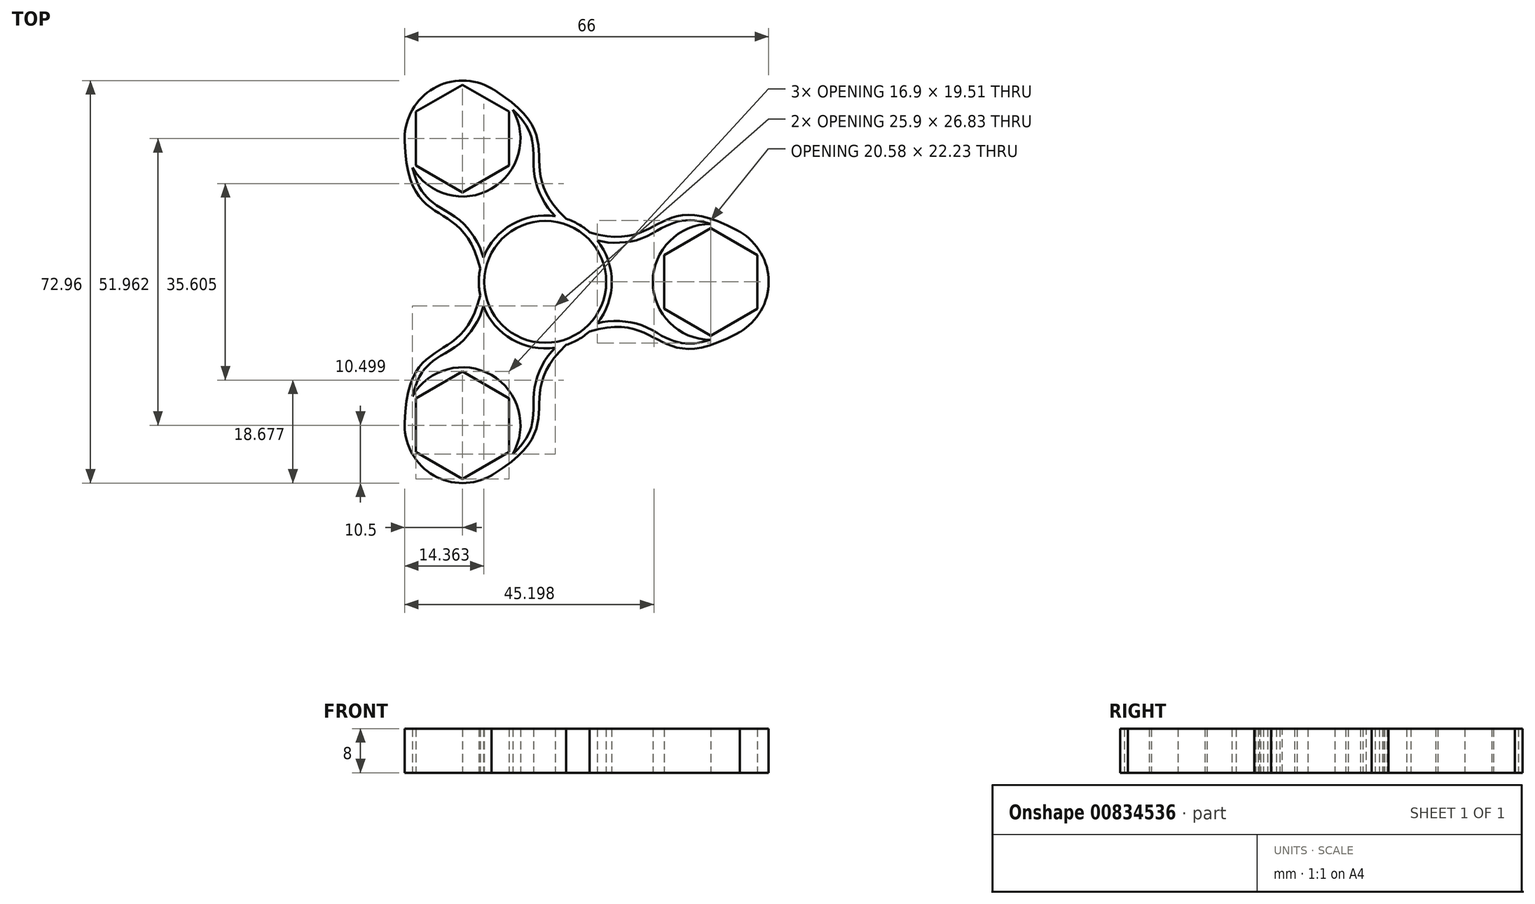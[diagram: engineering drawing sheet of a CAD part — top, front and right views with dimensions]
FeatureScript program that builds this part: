
annotation { "Feature Type Name" : "Feature", "Feature Type Description" : "" }
export const myFeature = defineFeature(function(context is Context, id is Id, definition is map)
    precondition{}
    {
        {
            var Q0;
            Q0=qCreatedBy(makeId("Top.planeOp"),FACE);
            var sketch = newSketch(context, id + "F0", { "sketchPlane" : qUnion([Q0])});
            skCircle(sketch, "E0", {"center": v(0, 0) * mm, "radius": 11.05 * mm});
            skCircle(sketch, "E1.cCircle", {"center": v(30, 0) * mm, "radius": 8.45 * mm, "construction": true});
            skLineSegment(sketch, "E1.0", {"start": v(30, 9.76) * mm, "end": v(38.45, 4.88) * mm});
            skLineSegment(sketch, "E1.1", {"start": v(38.45, 4.88) * mm, "end": v(38.45, -4.88) * mm});
            skLineSegment(sketch, "E1.2", {"start": v(38.45, -4.88) * mm, "end": v(30, -9.76) * mm});
            skLineSegment(sketch, "E1.3", {"start": v(30, -9.76) * mm, "end": v(21.55, -4.88) * mm});
            skLineSegment(sketch, "E1.4", {"start": v(21.55, -4.88) * mm, "end": v(21.55, 4.88) * mm});
            skLineSegment(sketch, "E1.5", {"start": v(21.55, 4.88) * mm, "end": v(30, 9.76) * mm});
            skPoint(sketch, "E1.0.midPoint", {"position": v(34.23, 7.32) * mm});
            skLineSegment(sketch, "E2.1.0", {"start": v(-15, 16.22) * mm, "end": v(-23.45, 21.1) * mm});
            skLineSegment(sketch, "E2.1.1", {"start": v(-6.55, 21.1) * mm, "end": v(-15, 16.22) * mm});
            skLineSegment(sketch, "E2.1.2", {"start": v(-23.45, 21.1) * mm, "end": v(-23.45, 30.86) * mm});
            skLineSegment(sketch, "E2.1.3", {"start": v(-23.45, 30.86) * mm, "end": v(-15, 35.74) * mm});
            skLineSegment(sketch, "E2.1.4", {"start": v(-15, 35.74) * mm, "end": v(-6.55, 30.86) * mm});
            skLineSegment(sketch, "E2.1.5", {"start": v(-6.55, 30.86) * mm, "end": v(-6.55, 21.1) * mm});
            skLineSegment(sketch, "E2.2.0", {"start": v(-6.55, -21.1) * mm, "end": v(-6.55, -30.86) * mm});
            skLineSegment(sketch, "E2.2.1", {"start": v(-15, -16.22) * mm, "end": v(-6.55, -21.1) * mm});
            skLineSegment(sketch, "E2.2.2", {"start": v(-6.55, -30.86) * mm, "end": v(-15, -35.74) * mm});
            skLineSegment(sketch, "E2.2.3", {"start": v(-15, -35.74) * mm, "end": v(-23.45, -30.86) * mm});
            skLineSegment(sketch, "E2.2.4", {"start": v(-23.45, -30.86) * mm, "end": v(-23.45, -21.1) * mm});
            skLineSegment(sketch, "E2.2.5", {"start": v(-23.45, -21.1) * mm, "end": v(-15, -16.22) * mm});
            skSolve(sketch);
        }
        {
            var Q0;
            Q0=qCreatedBy(makeId("Top.planeOp"),FACE);
            var sketch = newSketch(context, id + "F1", { "sketchPlane" : qUnion([Q0])});
            skLineSegment(sketch, "E3.0.0", {"start": v(-6.55, 21.1) * mm, "end": v(-6.55, 30.86) * mm});
            skLineSegment(sketch, "E3.0.1", {"start": v(-6.55, 30.86) * mm, "end": v(-15, 35.74) * mm});
            skLineSegment(sketch, "E3.0.2", {"start": v(-15, 35.74) * mm, "end": v(-23.45, 30.86) * mm});
            skLineSegment(sketch, "E3.0.3", {"start": v(-23.45, 30.86) * mm, "end": v(-23.45, 21.1) * mm});
            skLineSegment(sketch, "E3.0.4", {"start": v(-23.45, 21.1) * mm, "end": v(-15, 16.22) * mm});
            skLineSegment(sketch, "E3.0.5", {"start": v(-15, 16.22) * mm, "end": v(-6.55, 21.1) * mm});
            skCircle(sketch, "E4.0.0", {"center": v(0, 0) * mm, "radius": 11.05 * mm});
            skLineSegment(sketch, "E5.0.0", {"start": v(30, 9.76) * mm, "end": v(21.55, 4.88) * mm});
            skLineSegment(sketch, "E5.0.1", {"start": v(21.55, 4.88) * mm, "end": v(21.55, -4.88) * mm});
            skLineSegment(sketch, "E5.0.2", {"start": v(21.55, -4.88) * mm, "end": v(30, -9.76) * mm});
            skLineSegment(sketch, "E5.0.3", {"start": v(30, -9.76) * mm, "end": v(38.45, -4.88) * mm});
            skLineSegment(sketch, "E5.0.4", {"start": v(38.45, -4.88) * mm, "end": v(38.45, 4.88) * mm});
            skLineSegment(sketch, "E5.0.5", {"start": v(38.45, 4.88) * mm, "end": v(30, 9.76) * mm});
            skLineSegment(sketch, "E6.0.0", {"start": v(-15, -16.22) * mm, "end": v(-23.45, -21.1) * mm});
            skLineSegment(sketch, "E6.0.1", {"start": v(-23.45, -21.1) * mm, "end": v(-23.45, -30.86) * mm});
            skLineSegment(sketch, "E6.0.2", {"start": v(-23.45, -30.86) * mm, "end": v(-15, -35.74) * mm});
            skLineSegment(sketch, "E6.0.3", {"start": v(-15, -35.74) * mm, "end": v(-6.55, -30.86) * mm});
            skLineSegment(sketch, "E6.0.4", {"start": v(-6.55, -30.86) * mm, "end": v(-6.55, -21.1) * mm});
            skLineSegment(sketch, "E6.0.5", {"start": v(-6.55, -21.1) * mm, "end": v(-15, -16.22) * mm});
            skPoint(sketch, "E7.0", {"position": v(30, 0) * mm});
            skCircle(sketch, "E8", {"center": v(30, 0) * mm, "radius": 10.5 * mm});
            skLineSegment(sketch, "E9", {"start": v(34.23, 7.32) * mm, "end": v(35.25, 9.1) * mm, "construction": true});
            skCircle(sketch, "E10.0", {"center": v(0, 0) * mm, "radius": 12.05 * mm});
            skLineSegment(sketch, "E11", {"start": v(8.01, 9) * mm, "end": v(8.01, -9) * mm, "construction": true});
            skFitSpline(sketch, "E12", {"points": [v(8.01, 9) * mm, v(35.25, 9.1) * mm], "startDerivative": vector(40.61, -12.36) * mm, "endDerivative": vector(46.42, -25.85) * mm});
            skLineSegment(sketch, "E13", {"start": v(34.22, -7.32) * mm, "end": v(35.25, -9.1) * mm, "construction": true});
            skFitSpline(sketch, "E14", {"points": [v(8.01, -9) * mm, v(35.25, -9.1) * mm], "startDerivative": vector(40.61, 12.36) * mm, "endDerivative": vector(46.43, 25.85) * mm});
            skLineSegment(sketch, "E15", {"start": v(-6.55, -30.86) * mm, "end": v(-23.45, -21.1) * mm, "construction": true});
            skCircle(sketch, "E16", {"center": v(-15, -25.98) * mm, "radius": 10.5 * mm});
            skLineSegment(sketch, "E17", {"start": v(-11.8, -2.44) * mm, "end": v(3.79, -11.44) * mm, "construction": true});
            skLineSegment(sketch, "E18", {"start": v(-23.45, -25.98) * mm, "end": v(-25.5, -25.98) * mm, "construction": true});
            skLineSegment(sketch, "E19", {"start": v(-10.78, -33.3) * mm, "end": v(-9.75, -35.07) * mm, "construction": true});
            skFitSpline(sketch, "E20", {"points": [v(-25.5, -25.98) * mm, v(-11.8, -2.44) * mm], "startDerivative": vector(0.82, 53.13) * mm, "endDerivative": vector(9.6, 41.35) * mm});
            skLineSegment(sketch, "E21", {"start": v(-25.23, -8.27) * mm, "end": v(-19.23, -18.66) * mm, "construction": true});
            skFitSpline(sketch, "E22", {"points": [v(3.79, -11.44) * mm, v(-9.75, -35.07) * mm], "startDerivative": vector(-31.01, -28.99) * mm, "endDerivative": vector(-45.6, -27.28) * mm});
            skLineSegment(sketch, "E23", {"start": v(-6.55, -25.98) * mm, "end": v(5.45, -25.98) * mm, "construction": true});
            skLineSegment(sketch, "E24", {"start": v(25.77, 7.32) * mm, "end": v(19.78, 17.71) * mm, "construction": true});
            skLineSegment(sketch, "E25", {"start": v(25.77, -7.32) * mm, "end": v(19.77, -17.71) * mm, "construction": true});
            skLineSegment(sketch, "E26", {"start": v(-23.45, 21.1) * mm, "end": v(-6.55, 30.86) * mm, "construction": true});
            skCircle(sketch, "E27", {"center": v(-15, 25.98) * mm, "radius": 10.5 * mm});
            skLineSegment(sketch, "E28", {"start": v(-19.22, 18.66) * mm, "end": v(-25.23, 8.27) * mm, "construction": true});
            skLineSegment(sketch, "E29", {"start": v(-6.55, 25.98) * mm, "end": v(5.45, 25.98) * mm, "construction": true});
            skLineSegment(sketch, "E30", {"start": v(-10.78, 33.3) * mm, "end": v(-9.75, 35.07) * mm, "construction": true});
            skLineSegment(sketch, "E31", {"start": v(-23.45, 25.98) * mm, "end": v(-25.5, 25.98) * mm, "construction": true});
            skLineSegment(sketch, "E32", {"start": v(-11.8, 2.44) * mm, "end": v(3.79, 11.44) * mm, "construction": true});
            skFitSpline(sketch, "E33", {"points": [v(-9.75, 35.07) * mm, v(3.79, 11.44) * mm], "startDerivative": vector(45.6, -27.28) * mm, "endDerivative": vector(31.01, -28.99) * mm});
            skFitSpline(sketch, "E34", {"points": [v(-25.5, 25.98) * mm, v(-11.8, 2.44) * mm], "startDerivative": vector(0.82, -53.13) * mm, "endDerivative": vector(9.6, -41.35) * mm});
            skFitSpline(sketch, "E35.0", {"points": [v(-10.26, 34.22) * mm, v(-8.4, 33.1) * mm, v(-6.27, 31.55) * mm, v(-4.43, 29.68) * mm, v(-3.47, 28.36) * mm, v(-2.84, 27.12) * mm, v(-2.45, 25.91) * mm, v(-2.24, 24.69) * mm, v(-2.11, 23) * mm, v(-2.1, 20.75) * mm, v(-1.75, 18.21) * mm, v(-0.96, 16.03) * mm, v(0.26, 13.76) * mm, v(1.76, 11.96) * mm, v(3.1, 10.7) * mm]});
            skFitSpline(sketch, "E36.0", {"points": [v(-24.5, 26) * mm, v(-24.47, 23.83) * mm, v(-24.19, 21.2) * mm, v(-23.49, 18.67) * mm, v(-22.83, 17.19) * mm, v(-22.07, 16.02) * mm, v(-21.21, 15.08) * mm, v(-20.26, 14.29) * mm, v(-18.87, 13.33) * mm, v(-16.92, 12.18) * mm, v(-14.9, 10.62) * mm, v(-13.4, 8.85) * mm, v(-12.05, 6.65) * mm, v(-11.24, 4.46) * mm, v(-10.83, 2.67) * mm]});
            skFitSpline(sketch, "E37.0", {"points": [v(7.72, 8.04) * mm, v(9.48, 7.5) * mm, v(11.78, 7.1) * mm, v(14.36, 7.18) * mm, v(16.65, 7.59) * mm, v(19.01, 8.56) * mm, v(20.98, 9.67) * mm, v(22.5, 10.4) * mm, v(23.67, 10.83) * mm, v(24.9, 11.1) * mm, v(26.3, 11.18) * mm, v(27.92, 11) * mm, v(30.46, 10.34) * mm, v(32.87, 9.27) * mm, v(34.76, 8.22) * mm]});
            skFitSpline(sketch, "E38.0", {"points": [v(7.72, -8.04) * mm, v(9.48, -7.5) * mm, v(11.78, -7.1) * mm, v(14.36, -7.18) * mm, v(16.65, -7.59) * mm, v(19.01, -8.56) * mm, v(20.98, -9.67) * mm, v(22.5, -10.4) * mm, v(23.67, -10.83) * mm, v(24.9, -11.1) * mm, v(26.3, -11.18) * mm, v(27.92, -11) * mm, v(30.46, -10.34) * mm, v(32.87, -9.27) * mm, v(34.76, -8.22) * mm]});
            skFitSpline(sketch, "E39.0", {"points": [v(3.1, -10.7) * mm, v(1.76, -11.96) * mm, v(0.26, -13.76) * mm, v(-0.96, -16.03) * mm, v(-1.75, -18.21) * mm, v(-2.1, -20.75) * mm, v(-2.11, -23) * mm, v(-2.24, -24.69) * mm, v(-2.45, -25.91) * mm, v(-2.84, -27.12) * mm, v(-3.47, -28.36) * mm, v(-4.43, -29.68) * mm, v(-6.27, -31.55) * mm, v(-8.4, -33.1) * mm, v(-10.26, -34.22) * mm]});
            skFitSpline(sketch, "E40.0", {"points": [v(-24.5, -26) * mm, v(-24.47, -23.83) * mm, v(-24.19, -21.2) * mm, v(-23.49, -18.67) * mm, v(-22.83, -17.19) * mm, v(-22.07, -16.02) * mm, v(-21.21, -15.08) * mm, v(-20.26, -14.29) * mm, v(-18.87, -13.33) * mm, v(-16.92, -12.18) * mm, v(-14.9, -10.62) * mm, v(-13.4, -8.85) * mm, v(-12.05, -6.65) * mm, v(-11.24, -4.46) * mm, v(-10.83, -2.67) * mm]});
            skSolve(sketch);
        }
        {
            var Q0;
            {var subQ0=sQuery(id+"F1.wireOp",EDGE,"E20");var subQ1=sQuery(id+"F1.wireOp",EDGE,"E10.0");var subQ2=makeQuery(id+"F1.imprint","INTERSECT",VERTEX,{"derivedFrom":[subQ1,subQ0]});Q0=makeQuery(id+"F1.imprint","IMPRINT",FACE,{"disambiguationData":[TD([[makeQuery(id+"F1.imprint","IMPRINT",EDGE,{"disambiguationData":[TD([[subQ2,-1.0]])],"derivedFrom":subQ1}),-1.0]])]});}
            var Q1;
            {var subQ0=sQuery(id+"F1.wireOp",EDGE,"E22");var subQ1=sQuery(id+"F1.wireOp",EDGE,"E10.0");var subQ2=makeQuery(id+"F1.imprint","INTERSECT",VERTEX,{"derivedFrom":[subQ1,subQ0]});Q1=makeQuery(id+"F1.imprint","IMPRINT",FACE,{"disambiguationData":[TD([[makeQuery(id+"F1.imprint","IMPRINT",EDGE,{"disambiguationData":[TD([[subQ2,1.0]])],"derivedFrom":subQ1}),-1.0]])]});}
            var Q2;
            Q2=makeQuery(id+"F1.imprint","IMPRINT",FACE,{"disambiguationData":[TD([[makeQuery(id+"F1.imprint","IMPRINT",EDGE,{"derivedFrom":sQuery(id+"F1.wireOp",EDGE,"E4.0.0")}),-1.0]])]});
            var Q3;
            Q3=makeQuery(id+"F1.imprint","IMPRINT",FACE,{"disambiguationData":[TD([[makeQuery(id+"F1.imprint","IMPRINT",EDGE,{"derivedFrom":sQuery(id+"F1.wireOp",EDGE,"E6.0.0")}),-1.0]])]});
            var Q4;
            Q4=makeQuery(id+"F1.imprint","IMPRINT",FACE,{"disambiguationData":[TD([[makeQuery(id+"F1.imprint","IMPRINT",EDGE,{"derivedFrom":sQuery(id+"F1.wireOp",EDGE,"E5.0.0")}),-1.0]])]});
            var Q5;
            {var subQ0=sQuery(id+"F1.wireOp",EDGE,"E38.0");var subQ1=sQuery(id+"F1.wireOp",EDGE,"E8");var subQ2=makeQuery(id+"F1.imprint","INTERSECT",VERTEX,{"derivedFrom":[subQ1,subQ0]});Q5=makeQuery(id+"F1.imprint","IMPRINT",FACE,{"disambiguationData":[TD([[makeQuery(id+"F1.imprint","IMPRINT",EDGE,{"disambiguationData":[TD([[subQ2,-1.0]])],"derivedFrom":subQ1}),-1.0]])]});}
            var Q6;
            {var subQ0=sQuery(id+"F1.wireOp",EDGE,"E12");var subQ1=sQuery(id+"F1.wireOp",EDGE,"E8");var subQ2=makeQuery(id+"F1.imprint","INTERSECT",VERTEX,{"disambiguationData":[OD(1.0)],"derivedFrom":[subQ1,subQ0]});Q6=makeQuery(id+"F1.imprint","IMPRINT",FACE,{"disambiguationData":[TD([[makeQuery(id+"F1.imprint","IMPRINT",EDGE,{"disambiguationData":[TD([[subQ2,-1.0]])],"derivedFrom":subQ1}),-1.0]])]});}
            var Q7;
            {var subQ0=sQuery(id+"F1.wireOp",EDGE,"E34");var subQ1=sQuery(id+"F1.wireOp",EDGE,"E10.0");var subQ2=makeQuery(id+"F1.imprint","INTERSECT",VERTEX,{"derivedFrom":[subQ1,subQ0]});Q7=makeQuery(id+"F1.imprint","IMPRINT",FACE,{"disambiguationData":[TD([[makeQuery(id+"F1.imprint","IMPRINT",EDGE,{"disambiguationData":[TD([[subQ2,1.0]])],"derivedFrom":subQ1}),-1.0]])]});}
            var Q8;
            Q8=makeQuery(id+"F1.imprint","IMPRINT",FACE,{"disambiguationData":[TD([[makeQuery(id+"F1.imprint","IMPRINT",EDGE,{"derivedFrom":sQuery(id+"F1.wireOp",EDGE,"E3.0.0")}),-1.0]])]});
            var Q9;
            {var subQ0=sQuery(id+"F1.wireOp",EDGE,"E33");var subQ1=sQuery(id+"F1.wireOp",EDGE,"E10.0");var subQ2=makeQuery(id+"F1.imprint","INTERSECT",VERTEX,{"derivedFrom":[subQ1,subQ0]});Q9=makeQuery(id+"F1.imprint","IMPRINT",FACE,{"disambiguationData":[TD([[makeQuery(id+"F1.imprint","IMPRINT",EDGE,{"disambiguationData":[TD([[subQ2,-1.0]])],"derivedFrom":subQ1}),-1.0]])]});}
            extrude(context, id + "F2", {"entities" : qUnion([Q0, Q1, Q2, Q3, Q4, Q5, Q6, Q7, Q8, Q9]), "depth" : 8 * mm, "offsetDistance" : 25 * mm});
        }
    });
